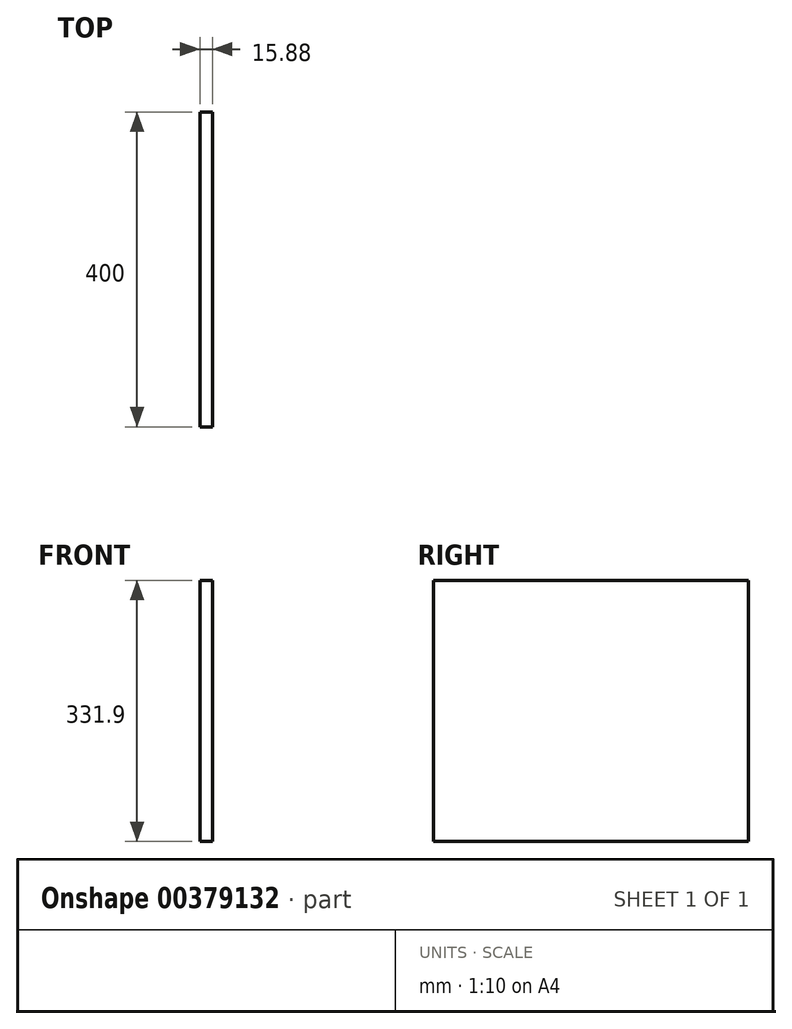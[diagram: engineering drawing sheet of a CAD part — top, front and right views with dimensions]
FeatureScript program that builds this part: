
annotation { "Feature Type Name" : "Feature", "Feature Type Description" : "" }
export const myFeature = defineFeature(function(context is Context, id is Id, definition is map)
    precondition{}
    {
        {
            var Q0;
            Q0=qCreatedBy(makeId("Front.planeOp"),FACE);
            var sketch = newSketch(context, id + "F0", { "sketchPlane" : qUnion([Q0])});
            skLineSegment(sketch, "E0.bottom", {"start": v(9.67, -165.96) * mm, "end": v(-6.21, -165.96) * mm});
            skLineSegment(sketch, "E0.top", {"start": v(9.67, 165.95) * mm, "end": v(-6.21, 165.95) * mm});
            skLineSegment(sketch, "E0.left", {"start": v(9.67, -165.96) * mm, "end": v(9.67, 165.95) * mm});
            skLineSegment(sketch, "E0.right", {"start": v(-6.21, -165.96) * mm, "end": v(-6.21, 165.95) * mm});
            skPoint(sketch, "E0.middle", {"position": v(1.73, 0) * mm});
            skSolve(sketch);
        }
        {
            var Q0;
            Q0=makeQuery(id+"F0.imprint","IMPRINT",FACE,{"disambiguationData":[TD([[makeQuery(id+"F0.imprint","IMPRINT",EDGE,{"derivedFrom":sQuery(id+"F0.wireOp",EDGE,"E0.bottom")}),-1.0]])]});
            extrude(context, id + "F1", {"entities" : qUnion([Q0]), "depth" : 400 * mm});
        }
    });
